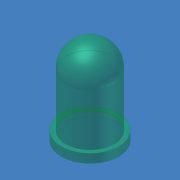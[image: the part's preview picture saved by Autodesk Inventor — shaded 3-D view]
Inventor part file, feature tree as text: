
AUTODESK INVENTOR PART (.ipt)
format: ipt  version: 2014 SP1 (Build 180222100, 222)  size: 126,464 bytes
history: native  units: mm (DEFAULTED — no unit token found)
features: revolve x1, sketch x1
ambient origin geometry x8: Origin, YZ Plane, XZ Plane, XY Plane, X Axis, Y Axis, Z Axis, Center Point
bodies: Solid1 (feature_tree)
feature tree (2):
  revolve  "Revolution1"  [1 undecoded]
  sketch  "Sketch1"  dims[d0=5.0mm d1=9.0mm d2=0.9mm d3=2.95mm d4=90.0deg]
note: 1 required parameter value undecoded (feature->parameter linkage not recoverable at this tier; creation-order binding heuristic only, values carry confidence <= 0.55)
